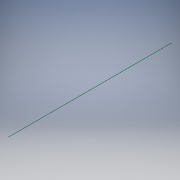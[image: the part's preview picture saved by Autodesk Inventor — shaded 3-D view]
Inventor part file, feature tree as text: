
AUTODESK INVENTOR PART (.ipt)
format: ipt  version: 2016 (Build 200138000, 138)  size: 107,008 bytes
history: native  units: in
note: dims shown in document units (in); Inventor stores cm internally (conversion verified against a paired STEP export)
features: extrude x1, sketch x1
ambient origin geometry x8: Origin, YZ Plane, XZ Plane, XY Plane, X Axis, Y Axis, Z Axis, Center Point
bodies: Solid1 (feature_tree)
feature tree (2):
  extrude  "Extrusion1"  Depth=787.4016in
  sketch  "Sketch1"  dims[d0=1.3386in d1=0.1181in d2=787.4016in d3=0.0in]
